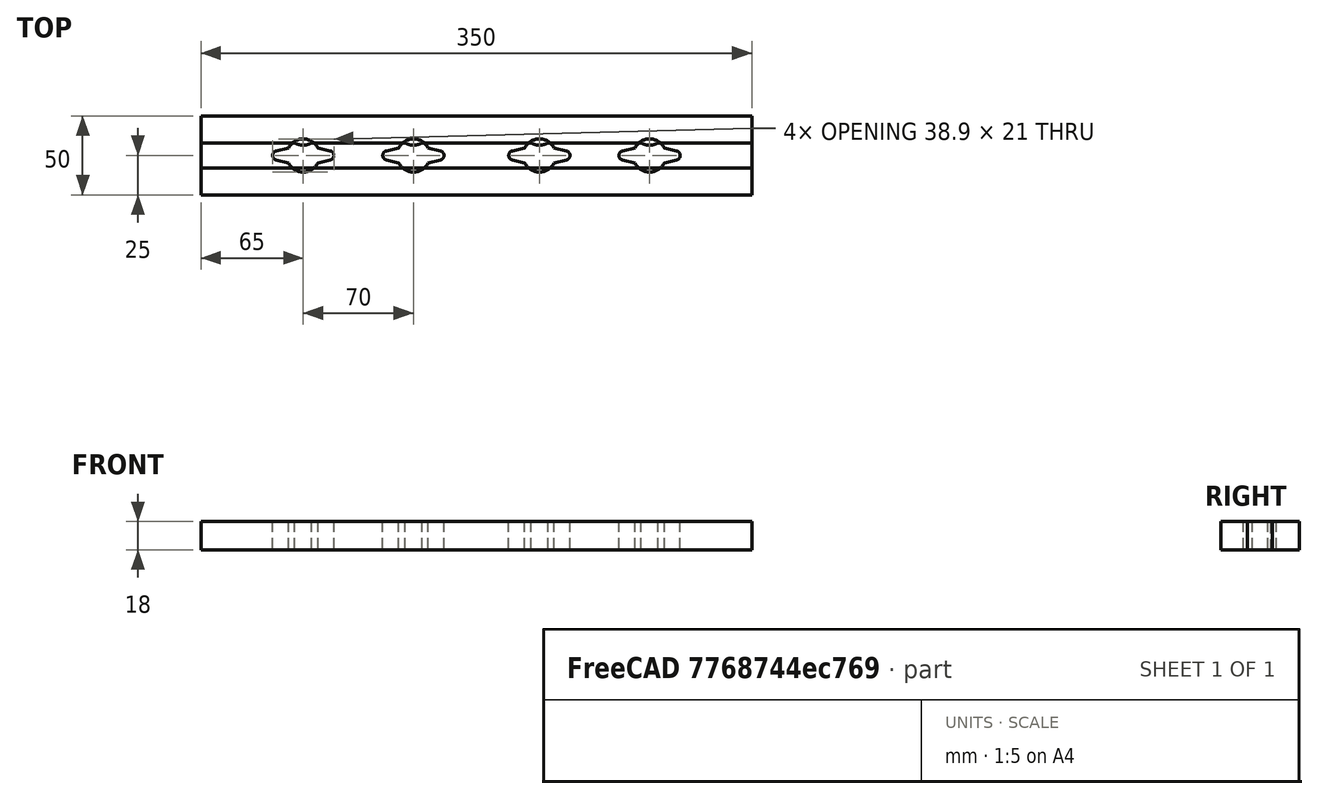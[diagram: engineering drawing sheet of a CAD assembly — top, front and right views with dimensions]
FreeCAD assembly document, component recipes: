
FREECAD ASSEMBLY — COMPONENT RECIPES ("conductor3")

This assembly document has 2 components, labeled P0..P1 below (a component is one placed body or linked part). 2 of them carry a construction recipe — the FreeCAD feature program that regenerates the part from scratch, quoted from this document or its linked companion documents; the rest are supplied as boundary geometry only. No exploded tour is included for this assembly.
COMPONENT P0 — recipe-attached ("Body", modeled in this document).
Construction recipe (the document's own serialized feature program — sketch geometry with constraints, then the solid features built on it; lengths are millimeters unless a unit is written):

FEATURE [PartDesign::CoordinateSystem] LCS_0
  AttacherType = Attacher::AttachEngine3D
  MapMode = 2
  Support = -> [X_Axis001]
FEATURE [PartDesign::SubShapeBinder] Binder
  BindCopyOnChange = 0
  BindMode = 0
  ClaimChildren = false
  Context = -> Body [Binder.]
  Fuse = false
  MakeFace = true
  OffsetFill = false
  OffsetIntersection = false
  OffsetJoinType = 0
  OffsetOpenResult = false
  PartialLoad = false
  Placement = pos=(110,-2.05e-14,2.05e-14) rot=(0,-1,0;3.14159rad)
  Relative = false
  Support = -> [<external dropper.FCStd>#Body[Pad.Sketch.]]
  _Version = 2
  expr: Placement = <<Sketch001>>.Placement
FEATURE [Sketcher::SketchObject] Sketch  label="Sketch_base_35mm"
  FullyConstrained = true
  MapMode = 5
  Support = -> [XY_Plane001]
  sketch-geometry (5):
    g0: LineSegment StartX=-175 StartY=-25 StartZ=0 EndX=-175 EndY=25 EndZ=0
    g1: LineSegment StartX=-175 StartY=25 StartZ=0 EndX=175 EndY=25 EndZ=0
    g2: LineSegment StartX=175 StartY=25 StartZ=0 EndX=175 EndY=-25 EndZ=0
    g3: LineSegment StartX=175 StartY=-25 StartZ=0 EndX=-175 EndY=-25 EndZ=0
    g4: GeomPoint X=0 Y=0 Z=0
  constraints (12):
    c: Coincident(g0,g1)
    c: Coincident(g1,g2)
    c: Coincident(g2,g3)
    c: Coincident(g3,g0)
    c: Horizontal(g1)
    c: Horizontal(g3)
    c: Vertical(g0)
    c: Vertical(g2)
    c: Symmetric(g1,g0,g4)
    c: Coincident(g4,g-1)
    c: DistanceX(g0,g1) = 350  'width'
    c: DistanceY(g2,g1) = 50  'length'
FEATURE [PartDesign::Plane] DatumPlane001
  AttachmentOffset = pos=(0,0,75) rot=(0,0,1;0rad)
  Length = 60
  MapMode = 5
  Placement = pos=(75,-1.67e-14,1.67e-14) rot=(0.57735,0.57735,0.57735;2.0944rad)
  ResizeMode = 0
  Support = -> [YZ_Plane001]
  Width = 60
  expr: .AttachmentOffset.Base.z = composit_full_size#<<main>>.modules_centres_dictance_x / 2
FEATURE [PartDesign::Plane] DatumPlane
  AttachmentOffset = pos=(0,0,35) rot=(0,0,1;0rad)
  Length = 60
  MapMode = 5
  Placement = pos=(110,-2.05e-14,2.05e-14) rot=(0.57735,0.57735,0.57735;2.0944rad)
  ResizeMode = 0
  Support = -> [DatumPlane001]
  Width = 60
  expr: .AttachmentOffset.Base.z = composit_full_size#<<dropper>>.distance_between_droppers2 / 2
FEATURE [Sketcher::SketchObject] Sketch001
  AttachmentOffset = pos=(0,0,0) rot=(0,0,1;-1.5708rad)
  FullyConstrained = true
  MapMode = 3
  Placement = pos=(110,-2.05e-14,2.05e-14) rot=(0,-1,0;3.14159rad)
  Support = -> [DatumPlane]
  sketch-geometry (1):
    g0: Circle CenterX=0 CenterY=0 CenterZ=0 NormalX=0 NormalY=0 NormalZ=1 AngleXU=0 Radius=2.5
  constraints (2):
    c: Coincident(g0,g-1)
    c: Diameter(g0) = 5
FEATURE [PartDesign::Pad] Pad
  Direction = (0,0,1)
  Length = 18
  Length2 = 10
  Profile = -> Sketch
  ReferenceAxis = -> Sketch [N_Axis]
  Type = 0
FEATURE [PartDesign::Pocket] Pocket
  BaseFeature = -> Pad
  Direction = (-1e-16,1e-16,1)
  Length = 5
  Length2 = 5
  Profile = -> Sketch001
  ReferenceAxis = -> Sketch001 [N_Axis]
  Type = 1
FEATURE [PartDesign::Pocket] Pocket001
  BaseFeature = -> Pocket
  Direction = (-1e-16,1e-16,1)
  Length = 5
  Length2 = 5
  Profile = -> Binder
  Type = 1
FEATURE [PartDesign::Mirrored] Mirrored
  MirrorPlane = -> Sketch001 [V_Axis]
FEATURE [PartDesign::Mirrored] Mirrored001
  MirrorPlane = -> XZ_Plane001
FEATURE [PartDesign::Mirrored] Mirrored002
  MirrorPlane = -> DatumPlane001
FEATURE [PartDesign::Mirrored] Mirrored003
  MirrorPlane = -> YZ_Plane001
FEATURE [PartDesign::MultiTransform] MultiTransform
  BaseFeature = -> Pocket001
  Originals = -> [Pocket,Pocket001]
  Transformations = -> [Mirrored,Mirrored001,Mirrored002,Mirrored003]
FEATURE [PartDesign::CoordinateSystem] Local_CS001
  AttacherType = Attacher::AttachEngine3D
  AttachmentOffset = pos=(0,0,18) rot=(0,0,1;0rad)
  MapMode = 5
  Placement = pos=(0,0,18) rot=(0,0,1;0rad)
  Support = -> [XY_Plane001]
  expr: .AttachmentOffset.Base.z = Pad.Length
FEATURE [PartDesign::Body] Body
  Group = -> [LCS_0,Binder,DatumPlane,Sketch,DatumPlane001,Sketch001,Pad,Pocket,Pocket001,MultiTransform,Mirrored,Mirrored001,Mirrored002,Mirrored003,Local_CS001]
  Origin = -> Origin001
  Tip = -> MultiTransform
COMPONENT P1 — recipe-attached ("Body001", modeled in this document).
Construction recipe (the document's own serialized feature program — sketch geometry with constraints, then the solid features built on it; lengths are millimeters unless a unit is written):

FEATURE [Sketcher::SketchObject] Sketch002
  FullyConstrained = true
  MapMode = 5
  Support = -> [XY_Plane002]
  expr: .Constraints.length = (<<Sketch_base_35mm>>.Constraints.length - Spreadsheet.tube_d) / 2
  sketch-geometry (5):
    g0: LineSegment StartX=-175 StartY=-8 StartZ=0 EndX=-175 EndY=8 EndZ=0
    g1: LineSegment StartX=-175 StartY=8 StartZ=0 EndX=175 EndY=8 EndZ=0
    g2: LineSegment StartX=175 StartY=8 StartZ=0 EndX=175 EndY=-8 EndZ=0
    g3: LineSegment StartX=175 StartY=-8 StartZ=0 EndX=-175 EndY=-8 EndZ=0
    g4: GeomPoint X=0 Y=0 Z=0
  constraints (12):
    c: Coincident(g0,g1)
    c: Coincident(g1,g2)
    c: Coincident(g2,g3)
    c: Coincident(g3,g0)
    c: Horizontal(g1)
    c: Horizontal(g3)
    c: Vertical(g0)
    c: Vertical(g2)
    c: Symmetric(g1,g0,g4)
    c: Coincident(g4,g-1)
    c: DistanceY(g2,g1) = 16  'length'
    c: DistanceX(g0,g1) = 350
FEATURE [PartDesign::Pad] Pad001
  Direction = (0,0,1)
  Length = 18
  Length2 = 10
  Profile = -> Sketch002
  ReferenceAxis = -> Sketch002 [N_Axis]
  Type = 0
FEATURE [PartDesign::Plane] DatumPlane002
  AttachmentOffset = pos=(110,-2.05e-14,2.05e-14) rot=(0.57735,0.57735,0.57735;2.0944rad)
  Length = 60
  MapMode = 5
  Placement = pos=(110,-2.05e-14,2.05e-14) rot=(0.57735,0.57735,0.57735;2.0944rad)
  ResizeMode = 0
  Support = -> [XY_Plane002]
  Width = 60
  expr: AttachmentOffset = DatumPlane.Placement
FEATURE [PartDesign::Plane] DatumPlane003
  AttachmentOffset = pos=(75,-1.67e-14,1.67e-14) rot=(0.57735,0.57735,0.57735;2.0944rad)
  Length = 60
  MapMode = 5
  Placement = pos=(75,-1.67e-14,1.67e-14) rot=(0.57735,0.57735,0.57735;2.0944rad)
  ResizeMode = 0
  Support = -> [XY_Plane002]
  Width = 60
  expr: AttachmentOffset = DatumPlane001.Placement
FEATURE [PartDesign::CoordinateSystem] Local_CS
  AttacherType = Attacher::AttachEngine3D
  AttachmentOffset = pos=(0,8,0) rot=(0,0,1;0rad)
  MapMode = 5
  Placement = pos=(0,8,0) rot=(0,0,1;0rad)
  Support = -> [XY_Plane002]
  expr: .AttachmentOffset.Base.y = Sketch002.Constraints.length / 2
FEATURE [Sketcher::SketchObject] Sketch003
  AttachmentOffset = pos=(110,17,0) rot=(0,0,1;3.14159rad)
  FullyConstrained = true
  MapMode = 5
  Placement = pos=(110,17,0) rot=(0,0,1;3.14159rad)
  Support = -> [XY_Plane002]
  expr: .AttachmentOffset.Base.x = DatumPlane002.Placement.Base.x
  expr: .AttachmentOffset.Base.y = Sketch002.Constraints.length / 2 + Spreadsheet.tube_d / 2
  sketch-geometry (1):
    g0: Circle CenterX=0 CenterY=0 CenterZ=0 NormalX=0 NormalY=0 NormalZ=1 AngleXU=0 Radius=3
  constraints (2):
    c: Coincident(g0,g-1)
    c: Diameter(g0) = 6
FEATURE [PartDesign::Pocket] Pocket002
  BaseFeature = -> Pad001
  Direction = (0,0,-1)
  Length = 5
  Length2 = 5
  Midplane = true
  Profile = -> Sketch003
  ReferenceAxis = -> Sketch003 [N_Axis]
  Type = 1
FEATURE [PartDesign::SubShapeBinder] Binder001
  BindCopyOnChange = 0
  BindMode = 0
  ClaimChildren = false
  Context = -> Body001 [Binder001.]
  Fuse = false
  MakeFace = true
  OffsetFill = false
  OffsetIntersection = false
  OffsetJoinType = 0
  OffsetOpenResult = false
  PartialLoad = false
  Placement = pos=(110,17,0) rot=(0,0,1;3.14159rad)
  Relative = false
  Support = -> [Body[Binder.]]
  _Version = 2
  expr: Placement = Sketch003.Placement
FEATURE [PartDesign::Pocket] Pocket003
  BaseFeature = -> Pocket002
  Direction = (0,0,-1)
  Length = 5
  Length2 = 5
  Midplane = true
  Profile = -> Binder001
  Type = 1
FEATURE [PartDesign::Mirrored] Mirrored004
  MirrorPlane = -> DatumPlane002
FEATURE [PartDesign::Mirrored] Mirrored005
  MirrorPlane = -> DatumPlane003
FEATURE [PartDesign::Mirrored] Mirrored006
  MirrorPlane = -> YZ_Plane002
FEATURE [PartDesign::MultiTransform] MultiTransform001
  BaseFeature = -> Pocket003
  Originals = -> [Pocket003]
  Transformations = -> [Mirrored004,Mirrored005,Mirrored006]
FEATURE [PartDesign::Body] Body001
  Group = -> [Sketch002,Pad001,DatumPlane002,DatumPlane003,Local_CS,Sketch003,Pocket002,Binder001,Pocket003,MultiTransform001,Mirrored004,Mirrored005,Mirrored006]
  Origin = -> Origin002
  Tip = -> MultiTransform001
PROVENANCE & LICENSES
A FreeCAD (.FCStd) document from a public repository crawl; recipes are the document's own serialized feature recipes (and, for linked parts, companion documents' recipes).
License: as declared in the source repository (recorded in the dataset sidecar).
